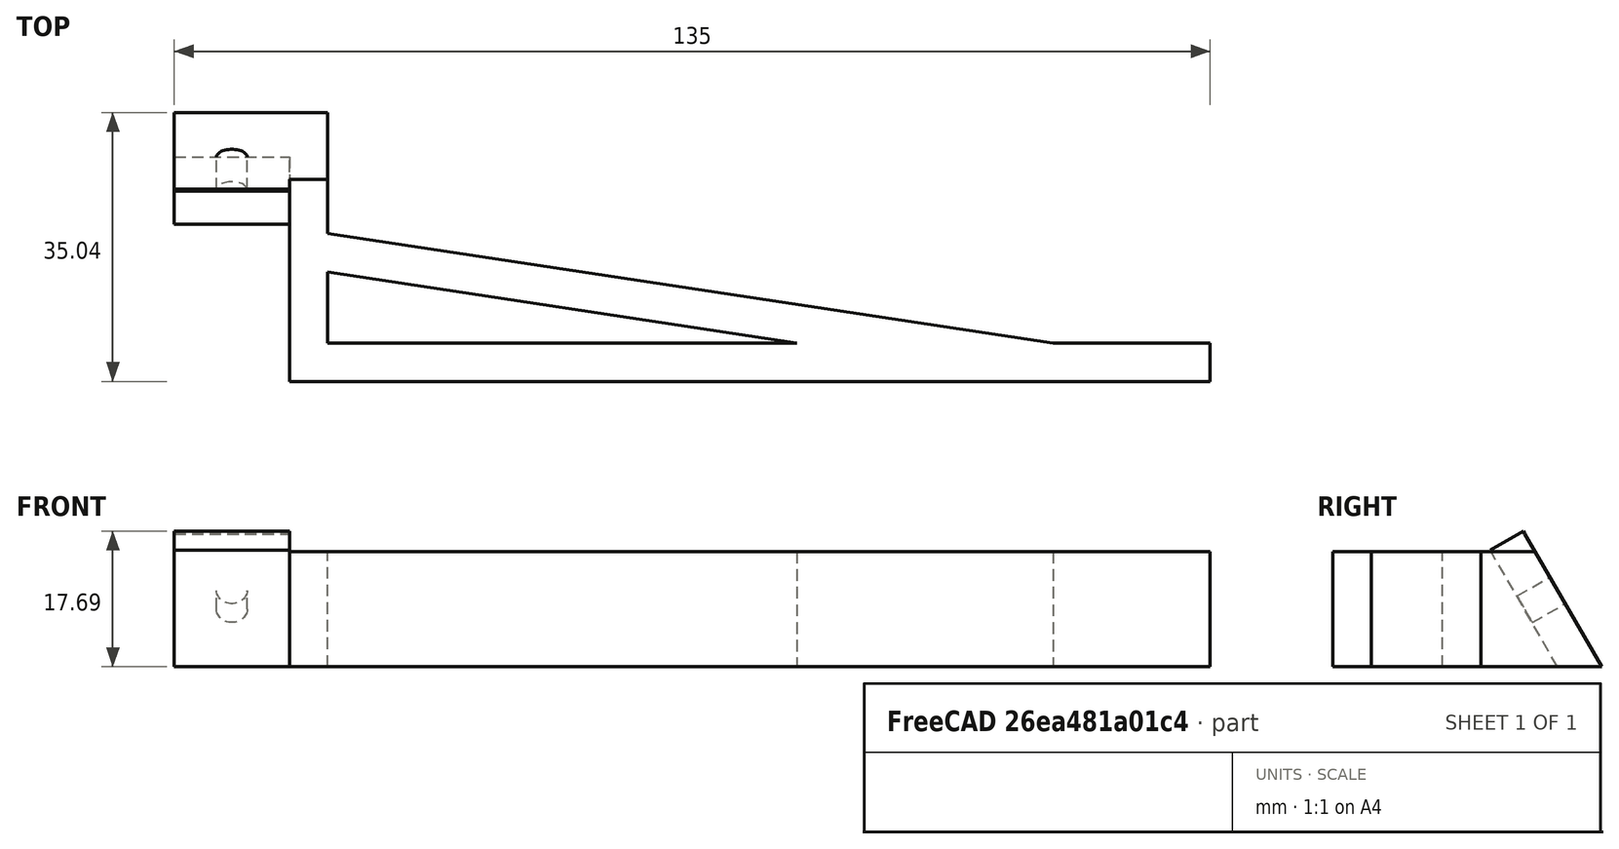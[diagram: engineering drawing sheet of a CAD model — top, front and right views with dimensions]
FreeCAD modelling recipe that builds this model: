
FCSTD DOCUMENT  (FreeCAD 0.14R3703 (Git))
Label: GOUM_Arm_Z_Probe
License: CC-BY 3.0
LicenseURL: http://creativecommons.org/licenses/by/3.0/
objects: Part::Box×6, Part::Cut×3, Part::Cylinder×1, Part::MultiFuse×1
note: 11 computed .brp shape members not serialized (recipe doc carries the construction recipe); baked Part::Feature solids carry a one-line shape summary decoded from their .brp

FEATURE [Part::Box] Box  label="Cube"
  Height = 15
  Length = 120
  Width = 5
FEATURE [Part::Box] Box001  label="Cube001"
  Height = 15
  Length = 5
  Width = 35
FEATURE [Part::Box] Box002  label="Cube002"
  Height = 21
  Length = 15
  Placement = pos=(-15,31,-3) rot=(1,0,0;0.523599rad)
  Width = 5
FEATURE [Part::Box] Box003  label="Cube003"
  Height = 20
  Length = 20
  Placement = pos=(-15,35,0) rot=(1,0,0;0.523599rad)
  Width = 10
FEATURE [Part::Box] Box004  label="Cube004"
  Height = 15
  Length = 100
  Placement = pos=(0,15,0) rot=(0,0,-1;0.150098rad)
  Width = 5
FEATURE [Part::Cylinder] Cylinder
  Angle = 360
  Height = 10
  Placement = pos=(-7.5,25,7.5) rot=(-1,0,0;1.0472rad)
  Radius = 2
FEATURE [Part::Box] Box005  label="Cube005"
  Height = 5
  Length = 20
  Placement = pos=(-15,25,-5) rot=(0,0,1;0rad)
  Width = 20
FEATURE [Part::MultiFuse] Fusion
  Shapes = -> [Box,Box001,Box002,Box004]
FEATURE [Part::Cut] Cut
  Base = -> Fusion
  Tool = -> Box005
FEATURE [Part::Cut] Cut001
  Base = -> Cut
  Tool = -> Box003
FEATURE [Part::Cut] Cut002  label="Z-Probe-release-strut"
  Base = -> Cut001
  Tool = -> Cylinder
